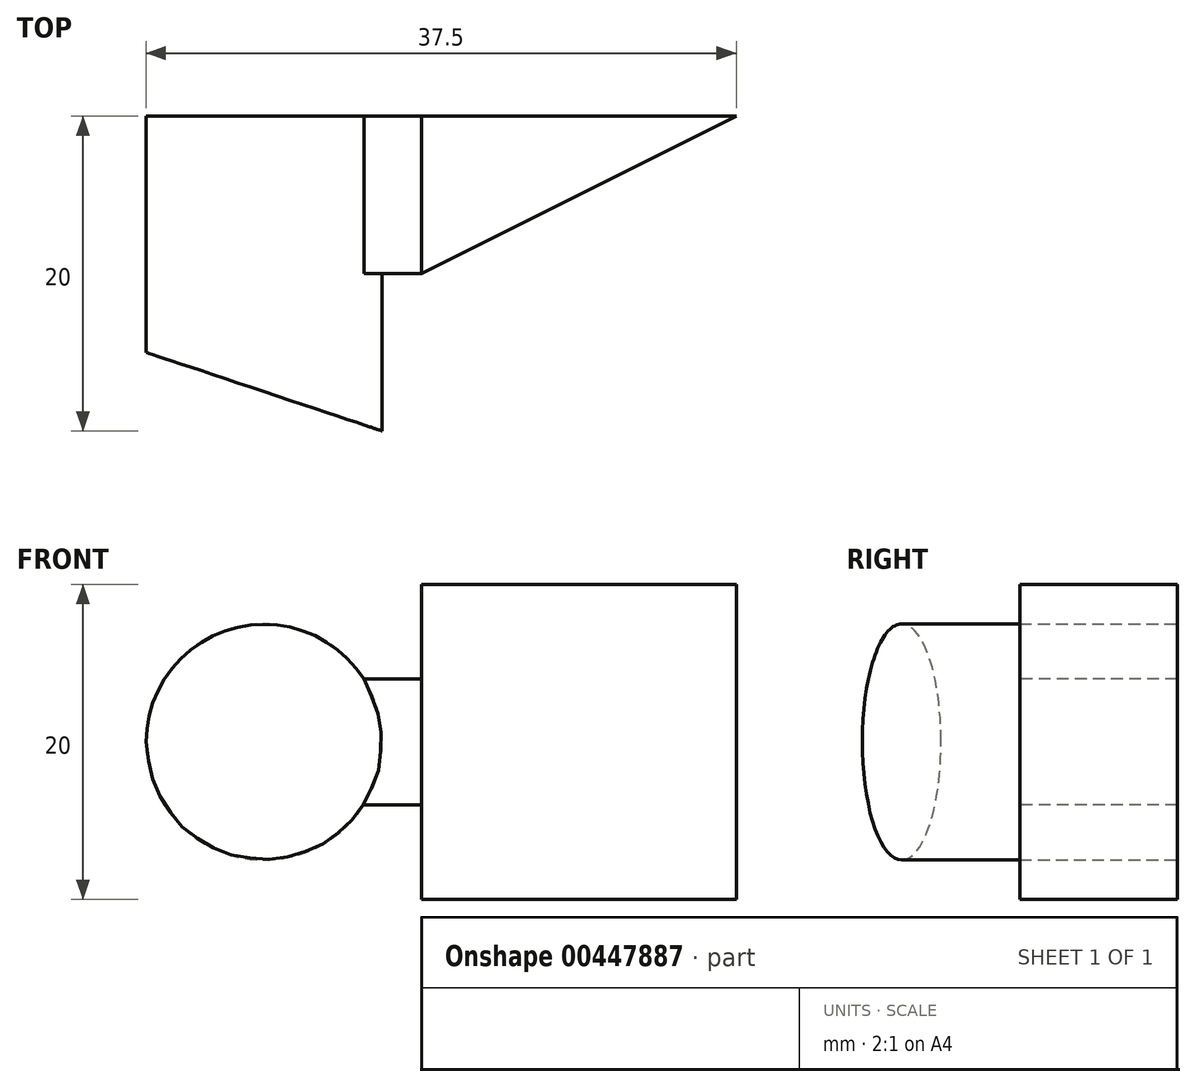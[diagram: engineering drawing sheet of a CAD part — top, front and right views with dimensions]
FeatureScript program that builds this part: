
annotation { "Feature Type Name" : "Feature", "Feature Type Description" : "" }
export const myFeature = defineFeature(function(context is Context, id is Id, definition is map)
    precondition{}
    {
        {
            var Q0;
            Q0=qCreatedBy(makeId("Top.planeOp"),FACE);
            var sketch = newSketch(context, id + "F0", { "sketchPlane" : qUnion([Q0])});
            skLineSegment(sketch, "E0.bottom", {"start": v(20, 5) * mm, "end": v(-20, 5) * mm});
            skLineSegment(sketch, "E0.top", {"start": v(20, -5) * mm, "end": v(-20, -5) * mm});
            skLineSegment(sketch, "E0.left", {"start": v(20, 5) * mm, "end": v(20, -5) * mm});
            skLineSegment(sketch, "E0.right", {"start": v(-20, 5) * mm, "end": v(-20, -5) * mm});
            skPoint(sketch, "E0.middle", {"position": v(0, 0) * mm});
            skSolve(sketch);
        }
        {
            var Q0;
            Q0 = qSketchRegion(id + "F0", true);
            extrude(context, id + "F1", {"entities" : qUnion([Q0]), "depth" : 20 * mm});
        }
        {
            var Q0;
            Q0=makeQuery(id+"F1.opExtrude","CAP_FACE",FACE,{"disambiguationData":[OSD([sQuery(id+"F0.wireOp",EDGE,"E0.bottom"),sQuery(id+"F0.wireOp",EDGE,"E0.top"),sQuery(id+"F0.wireOp",EDGE,"E0.left"),sQuery(id+"F0.wireOp",EDGE,"E0.right")])],"isStart":false});
            var sketch = newSketch(context, id + "F2", { "sketchPlane" : qUnion([Q0])});
            skLineSegment(sketch, "E1", {"start": v(20, 5) * mm, "end": v(0, -5) * mm});
            skLineSegment(sketch, "E2", {"start": v(0, -5) * mm, "end": v(20, -5) * mm});
            skLineSegment(sketch, "E3", {"start": v(20, -5) * mm, "end": v(20, 5) * mm});
            skSolve(sketch);
        }
        {
            var Q0;
            Q0 = qSketchRegion(id + "F2", true);
            extrude(context, id + "F3", {"entities" : qUnion([Q0]), "operationType" : NewBodyOperationType.REMOVE, "endBound" : BoundingType.THROUGH_ALL, "oppositeDirection" : true, "depth" : 25 * mm});
        }
        {
            var Q0;
            Q0=makeQuery(id+"F1.opExtrude","SWEPT_FACE",FACE,{"disambiguationData":[OSD([sQuery(id+"F0.wireOp",EDGE,"E0.top")])]});
            var sketch = newSketch(context, id + "F4", { "sketchPlane" : qUnion([Q0])});
            skPoint(sketch, "E4", {"position": v(-10, 10) * mm});
            skPoint(sketch, "E4.positionSnap0", {"position": v(-20, 10) * mm});
            skPoint(sketch, "E4.positionSnap1", {"position": v(-10, 20) * mm});
            skCircle(sketch, "E5", {"center": v(-10, 10) * mm, "radius": 7.5 * mm});
            skSolve(sketch);
        }
        {
            var Q0;
            Q0 = qSketchRegion(id + "F4", true);
            extrude(context, id + "F5", {"entities" : qUnion([Q0]), "operationType" : NewBodyOperationType.ADD, "depth" : 10 * mm});
        }
        {
            var Q0;
            Q0=qCreatedBy(makeId("Top.planeOp"),FACE);
            var sketch = newSketch(context, id + "F6", { "sketchPlane" : qUnion([Q0])});
            skLineSegment(sketch, "E6", {"start": v(0, 0) * mm, "end": v(0, -5) * mm});
            skLineSegment(sketch, "E7", {"start": v(0, -5) * mm, "end": v(-2.5, -5) * mm});
            skLineSegment(sketch, "E8", {"start": v(-2.5, -5) * mm, "end": v(-2.5, -15) * mm});
            skLineSegment(sketch, "E9", {"start": v(-17.5, -10) * mm, "end": v(-2.5, -15) * mm});
            skLineSegment(sketch, "E10", {"start": v(-2.5, -15) * mm, "end": v(-17.5, -15) * mm});
            skLineSegment(sketch, "E11", {"start": v(-17.5, -15) * mm, "end": v(-17.5, -10) * mm});
            skSolve(sketch);
        }
        {
            var Q0;
            Q0 = qSketchRegion(id + "F6", true);
            extrude(context, id + "F7", {"entities" : qUnion([Q0]), "operationType" : NewBodyOperationType.REMOVE, "depth" : 25 * mm});
        }
        {
            var Q0;
            Q0 = qSketchRegion(id + "F6", true);
            extrude(context, id + "F8", {"entities" : qUnion([Q0]), "operationType" : NewBodyOperationType.REMOVE, "endBound" : BoundingType.THROUGH_ALL, "depth" : 25 * mm});
        }
        {
            var Q0;
            Q0=makeQuery(id+"F1.opExtrude","SWEPT_FACE",FACE,{"disambiguationData":[OSD([sQuery(id+"F0.wireOp",EDGE,"E0.top")])]});
            var sketch = newSketch(context, id + "F9", { "sketchPlane" : qUnion([Q0])});
            skPoint(sketch, "E12", {"position": v(0, 14) * mm});
            skPoint(sketch, "E13", {"position": v(0, 6) * mm});
            skLineSegment(sketch, "E14", {"start": v(0, 14) * mm, "end": v(-3.66, 14) * mm});
            skLineSegment(sketch, "E15", {"start": v(0, 6) * mm, "end": v(-3.66, 6) * mm});
            skLineSegment(sketch, "E16", {"start": v(0, 6) * mm, "end": v(0, 0) * mm});
            skLineSegment(sketch, "E17", {"start": v(0, 0) * mm, "end": v(-20, 0) * mm});
            skLineSegment(sketch, "E18", {"start": v(-20, 0) * mm, "end": v(-20, 20) * mm});
            skLineSegment(sketch, "E19", {"start": v(-20, 20) * mm, "end": v(0, 20) * mm});
            skLineSegment(sketch, "E20", {"start": v(0, 20) * mm, "end": v(0, 14) * mm});
            skArc(sketch, "E21", {"start": v(-3.66, 14) * mm, "mid": v(-17.5, 10) * mm, "end": v(-3.66, 6) * mm});
            skSolve(sketch);
        }
        {
            var Q0;
            Q0 = qSketchRegion(id + "F9", true);
            extrude(context, id + "F10", {"entities" : qUnion([Q0]), "operationType" : NewBodyOperationType.REMOVE, "endBound" : BoundingType.THROUGH_ALL, "oppositeDirection" : true, "depth" : 25 * mm});
        }
    });
